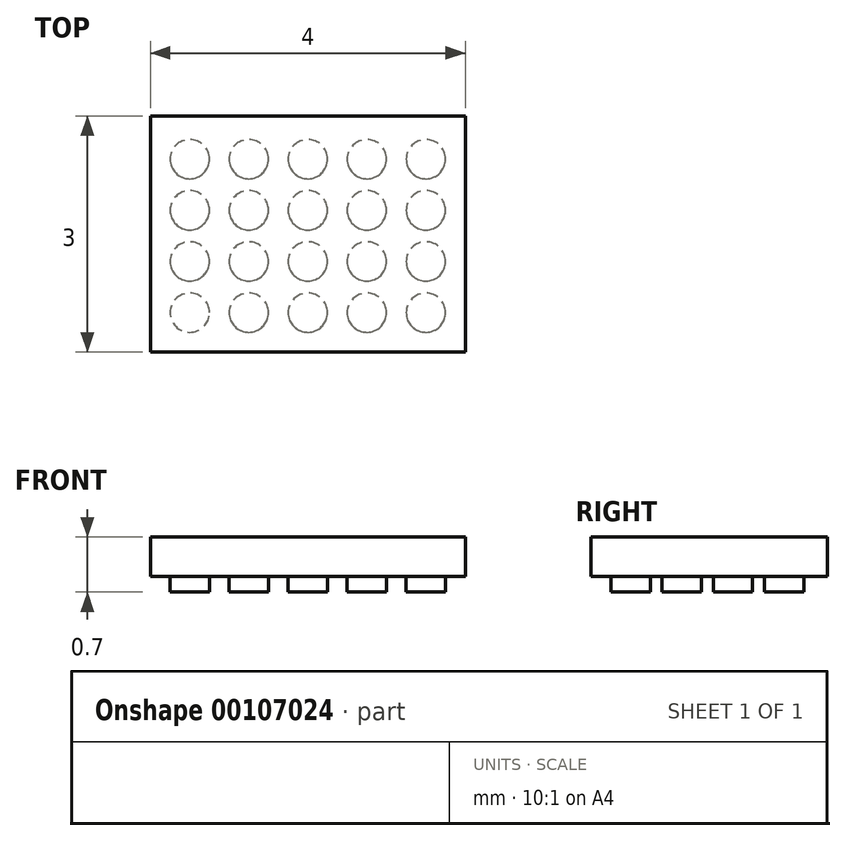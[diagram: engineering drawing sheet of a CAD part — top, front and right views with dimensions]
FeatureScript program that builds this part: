
annotation { "Feature Type Name" : "Feature", "Feature Type Description" : "" }
export const myFeature = defineFeature(function(context is Context, id is Id, definition is map)
    precondition{}
    {
        {
            var Q0;
            Q0=qCreatedBy(makeId("Top.planeOp"),FACE);
            var sketch = newSketch(context, id + "F0", { "sketchPlane" : qUnion([Q0])});
            skLineSegment(sketch, "E0.bottom", {"start": v(0, 0) * mm, "end": v(4, 0) * mm});
            skLineSegment(sketch, "E0.top", {"start": v(0, 3) * mm, "end": v(4, 3) * mm});
            skLineSegment(sketch, "E0.left", {"start": v(0, 0) * mm, "end": v(0, 3) * mm});
            skLineSegment(sketch, "E0.right", {"start": v(4, 0) * mm, "end": v(4, 3) * mm});
            skSolve(sketch);
        }
        {
            var Q0;
            Q0 = qSketchRegion(id + "F0", true);
            extrude(context, id + "F1", {"entities" : qUnion([Q0]), "depth" : .5 * mm});
        }
        {
            var Q0;
            Q0=makeQuery(id+"F1.opExtrude","CAP_FACE",FACE,{"disambiguationData":[OSD([sQuery(id+"F0.wireOp",EDGE,"E0.bottom"),sQuery(id+"F0.wireOp",EDGE,"E0.top"),sQuery(id+"F0.wireOp",EDGE,"E0.left"),sQuery(id+"F0.wireOp",EDGE,"E0.right")])],"isStart":true});
            var sketch = newSketch(context, id + "F2", { "sketchPlane" : qUnion([Q0])});
            skCircle(sketch, "E1", {"center": v(0.5, -0.5) * mm, "radius": 0.25 * mm});
            skCircle(sketch, "E2.1.0.0", {"center": v(1.25, -0.5) * mm, "radius": 0.25 * mm});
            skCircle(sketch, "E2.2.0.0", {"center": v(2, -0.5) * mm, "radius": 0.25 * mm});
            skCircle(sketch, "E2.3.0.0", {"center": v(2.75, -0.5) * mm, "radius": 0.25 * mm});
            skCircle(sketch, "E2.4.0.0", {"center": v(3.5, -0.5) * mm, "radius": 0.25 * mm});
            skLineSegment(sketch, "E2.direction1", {"start": v(0.5, -0.5) * mm, "end": v(1.25, -0.5) * mm, "construction": true});
            skCircle(sketch, "E3.0.1.0", {"center": v(2, -1.15) * mm, "radius": 0.25 * mm});
            skCircle(sketch, "E3.0.1.1", {"center": v(2.75, -1.15) * mm, "radius": 0.25 * mm});
            skCircle(sketch, "E3.0.1.2", {"center": v(3.5, -1.15) * mm, "radius": 0.25 * mm});
            skCircle(sketch, "E3.0.1.3", {"center": v(0.5, -1.15) * mm, "radius": 0.25 * mm});
            skCircle(sketch, "E3.0.1.4", {"center": v(1.25, -1.15) * mm, "radius": 0.25 * mm});
            skLineSegment(sketch, "E3.0.1.5", {"start": v(0.5, -1.15) * mm, "end": v(1.25, -1.15) * mm, "construction": true});
            skCircle(sketch, "E3.0.2.0", {"center": v(2, -1.8) * mm, "radius": 0.25 * mm});
            skCircle(sketch, "E3.0.2.1", {"center": v(2.75, -1.8) * mm, "radius": 0.25 * mm});
            skCircle(sketch, "E3.0.2.2", {"center": v(3.5, -1.8) * mm, "radius": 0.25 * mm});
            skCircle(sketch, "E3.0.2.3", {"center": v(0.5, -1.8) * mm, "radius": 0.25 * mm});
            skCircle(sketch, "E3.0.2.4", {"center": v(1.25, -1.8) * mm, "radius": 0.25 * mm});
            skLineSegment(sketch, "E3.0.2.5", {"start": v(0.5, -1.8) * mm, "end": v(1.25, -1.8) * mm, "construction": true});
            skCircle(sketch, "E3.0.3.0", {"center": v(2, -2.45) * mm, "radius": 0.25 * mm});
            skCircle(sketch, "E3.0.3.1", {"center": v(2.75, -2.45) * mm, "radius": 0.25 * mm});
            skCircle(sketch, "E3.0.3.2", {"center": v(3.5, -2.45) * mm, "radius": 0.25 * mm});
            skCircle(sketch, "E3.0.3.3", {"center": v(0.5, -2.45) * mm, "radius": 0.25 * mm});
            skCircle(sketch, "E3.0.3.4", {"center": v(1.25, -2.45) * mm, "radius": 0.25 * mm});
            skLineSegment(sketch, "E3.0.3.5", {"start": v(0.5, -2.45) * mm, "end": v(1.25, -2.45) * mm, "construction": true});
            skLineSegment(sketch, "E3.direction1", {"start": v(0.5, -0.5) * mm, "end": v(-24.5, -0.5) * mm, "construction": true});
            skLineSegment(sketch, "E3.direction2", {"start": v(0.5, -0.5) * mm, "end": v(0.5, -1.15) * mm, "construction": true});
            skSolve(sketch);
        }
        {
            var Q0;
            Q0 = qSketchRegion(id + "F2", true);
            extrude(context, id + "F3", {"entities" : qUnion([Q0]), "operationType" : NewBodyOperationType.ADD, "depth" : .2 * mm});
        }
    });
